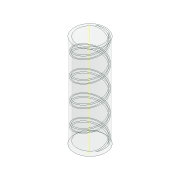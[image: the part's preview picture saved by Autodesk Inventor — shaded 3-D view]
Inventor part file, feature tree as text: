
AUTODESK INVENTOR PART (.ipt)
format: ipt  version: 2020.4 (Build 244396000, 396)  size: 431,104 bytes
history: native  units: in
note: dims shown in document units (in); Inventor stores cm internally (conversion verified against a paired STEP export)
features: extrude x2, helix x1, sketch x1, projected_geometry x1
ambient origin geometry x8: Origin, YZ Plane, XZ Plane, XY Plane, X Axis, Y Axis, Z Axis, Center Point
bodies: Solid1 (feature_tree)
feature tree (5):
  extrude  "Extrusion1"  Depth=0.125in
  extrude  "Extrusion2"  Depth=0.3in
  helix  "Coil1"  [1 undecoded]
  sketch  "Sketch2"  dims[d0=1.225in d1=0.125in d2=0.3in d3=0.0625in d4=0.125in d5=0.0in d6=4.375in d7=0.0in d8=1.0in d9=4.25in d10=0.3937in d11=0.0in d12=90.0deg d13=90.0deg d14=0.0in d15=0.0in]
  projected_geometry  "Projected Loop1"
note: 1 required parameter value undecoded (feature->parameter linkage not recoverable at this tier; creation-order binding heuristic only, values carry confidence <= 0.55)
